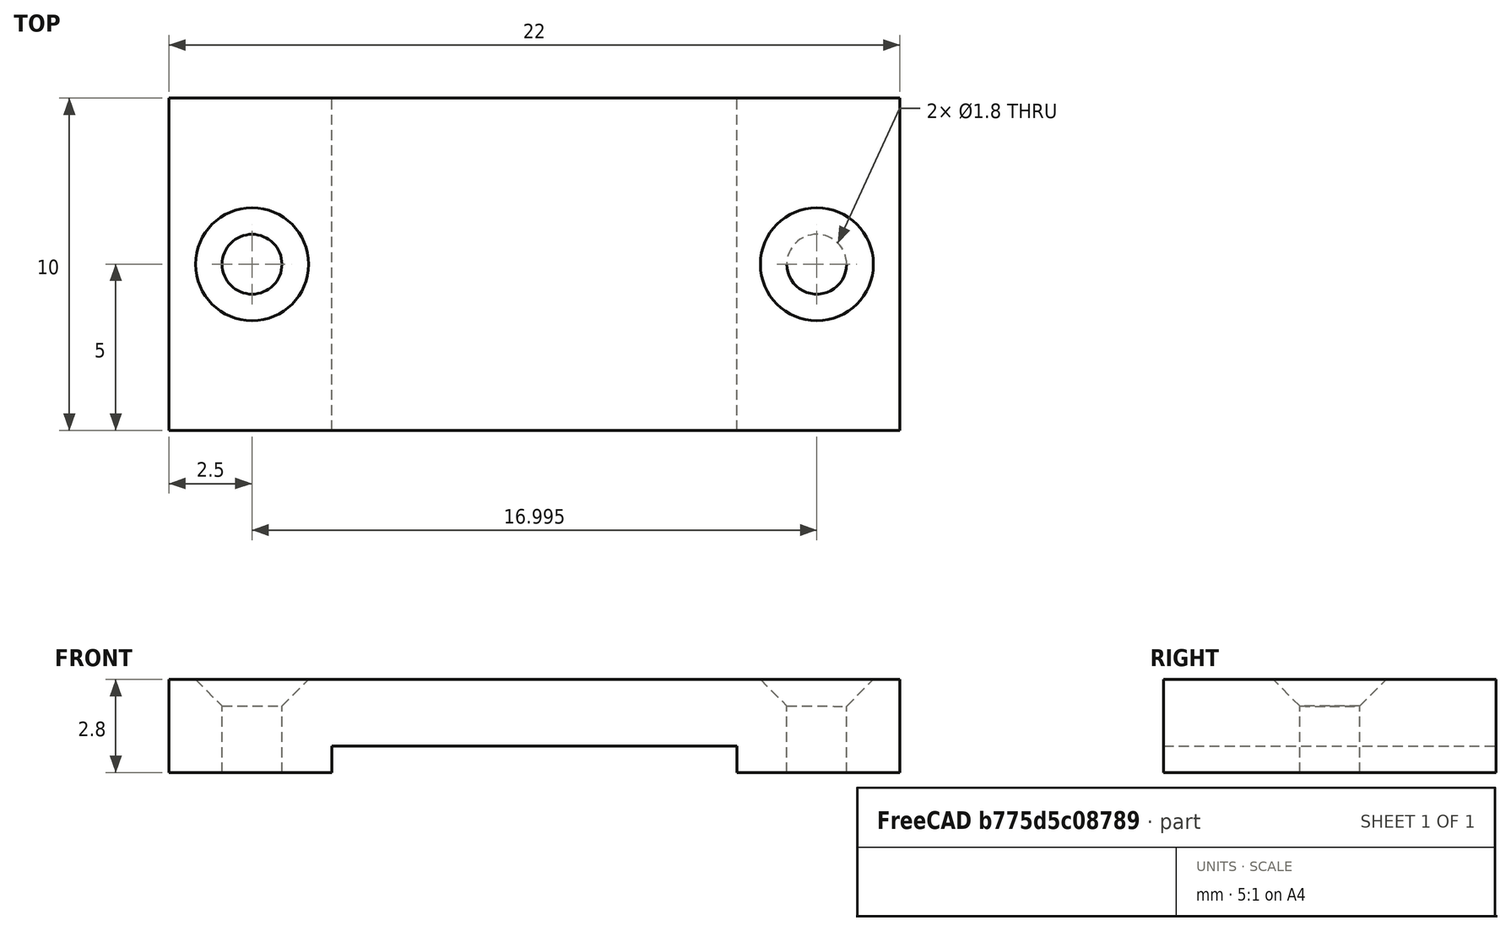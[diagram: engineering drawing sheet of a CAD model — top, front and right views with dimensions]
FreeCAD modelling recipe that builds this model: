
FCSTD DOCUMENT  (FreeCAD 0.17R13522 (Git))
Label: sujetador_boton
License: CreativeCommons Attribution-ShareAlike
LicenseURL: http://creativecommons.org/licenses/by-sa/4.0/
objects: Part::Cut×9, Part::Box×3, Part::Feature×3, Part::Part2DObjectPython×2, Part::Extrusion×2, Part::Chamfer×2, Part::Cylinder×2
note: 23 computed .brp shape members not serialized (recipe doc carries the construction recipe); baked Part::Feature solids carry a one-line shape summary decoded from their .brp

FEATURE [Part::Box] Box  label="base"
  AttacherType = Attacher::AttachEngine3D
  Height = 2.8
  Length = 22
  Width = 12
FEATURE [Part::Part2DObjectPython] Circle  # Draft 2D object (typed FeaturePython)
  FirstAngle = 0
  LastAngle = 0
  MakeFace = true
  Placement = pos=(2.5,6,2.8) rot=(0,0,1;3.14159rad)
  Radius = 0.7
FEATURE [Part::Extrusion] Extrude
  Base = -> Circle
  Dir = (0,0,1)
  DirMode = 2
  FaceMakerClass = Part::FaceMakerBullseye
  LengthFwd = 10
  LengthRev = 0
  Placement = pos=(0,0,-6) rot=(0,0,1;0rad)
  Solid = false
  Symmetric = false
FEATURE [Part::Part2DObjectPython] Circle001  # Draft 2D object (typed FeaturePython)
  FirstAngle = 0
  LastAngle = 0
  MakeFace = true
  Placement = pos=(19.5,6,2.8) rot=(0,0,1;3.14159rad)
  Radius = 0.7
FEATURE [Part::Extrusion] Extrude001
  Base = -> Circle001
  Dir = (0,0,1)
  DirMode = 2
  FaceMakerClass = Part::FaceMakerBullseye
  LengthFwd = 10
  LengthRev = 0
  Placement = pos=(0,0,-6) rot=(0,0,1;0rad)
  Solid = false
  Symmetric = false
FEATURE [Part::Cut] Cut
  Base = -> Box
  Refine = true
  Tool = -> Extrude
FEATURE [Part::Cut] Cut001
  Base = -> Cut
  Refine = true
  Tool = -> Extrude001
FEATURE [Part::Chamfer] Chamfer
  Base = -> Cut001
  Edges = 1 edges r=1: [Edge10]
FEATURE [Part::Chamfer] Chamfer001
  Base = -> Chamfer
  Edges = 1 edges r=1: [Edge6]
FEATURE [Part::Box] Box001  label="Cube"
  AttacherType = Attacher::AttachEngine3D
  Height = 10
  Length = 12.2
  Placement = pos=(4.9,0,-9.2) rot=(0,0,1;0rad)
  Width = 12
FEATURE [Part::Cut] Cut002  label="sujetador boton"
  Base = -> Chamfer001
  Refine = true
  Tool = -> Box001
FEATURE [Part::Cylinder] Cylinder
  Angle = 360
  AttacherType = Attacher::AttachEngine3D
  Height = 30
  Placement = pos=(2.5,6,-7.1) rot=(0,0,1;0rad)
  Radius = 0.7
FEATURE [Part::Feature] Cylinder001
  Placement = pos=(19.55,6,-11) rot=(0,0,1;0rad)
  shape: bbox 1.4 x 1.4 x 30 mm, 3 faces (baked)
FEATURE [Part::Cut] Cut003
  Base = -> Cut002
  Refine = true
  Tool = -> Cylinder
FEATURE [Part::Cut] Cut004
  Base = -> Cut003
  Refine = true
  Tool = -> Cylinder001
FEATURE [Part::Box] Box002  label="Cube001"
  AttacherType = Attacher::AttachEngine3D
  Height = 20
  Length = 30
  Placement = pos=(-3,0,-6) rot=(0,0,1;0rad)
  Width = 1
FEATURE [Part::Feature] Box002001  label="Cube002"
  Placement = pos=(-3,11,-6) rot=(0,0,1;0rad)
  shape: bbox 30 x 1 x 20 mm, 6 faces (baked)
FEATURE [Part::Cut] Cut005
  Base = -> Cut004
  Refine = true
  Tool = -> Box002
FEATURE [Part::Cut] Cut006
  Base = -> Cut005
  Refine = true
  Tool = -> Box002001
FEATURE [Part::Cylinder] Cylinder002
  Angle = 360
  AttacherType = Attacher::AttachEngine3D
  Height = 25
  Placement = pos=(2.5,6,-11) rot=(0,0,1;0rad)
  Radius = 0.9
FEATURE [Part::Feature] Cylinder002001  label="Cylinder003"
  Placement = pos=(19.4946,6,-22.6254) rot=(0,0,1;0rad)
  shape: bbox 1.8 x 1.8 x 25 mm, 3 faces (baked)
FEATURE [Part::Cut] Cut007
  Base = -> Cut006
  Placement = pos=(0,0,-9) rot=(0,0,1;0rad)
  Refine = true
  Tool = -> Cylinder002
FEATURE [Part::Cut] Cut008
  Base = -> Cut007
  Refine = true
  Tool = -> Cylinder002001
